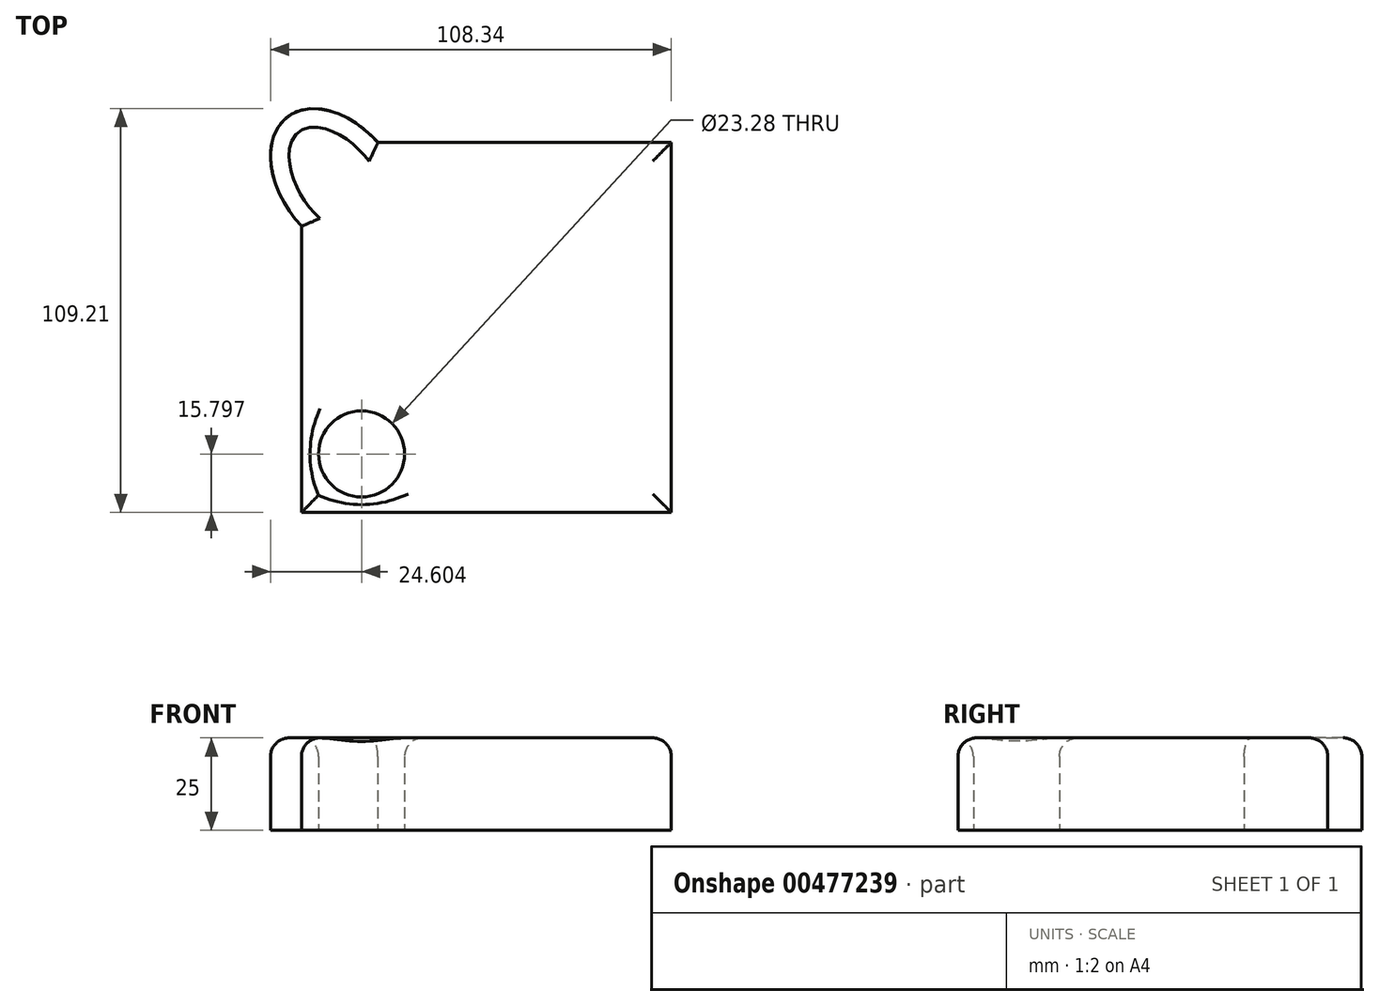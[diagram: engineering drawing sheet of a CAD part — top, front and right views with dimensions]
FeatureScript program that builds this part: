
annotation { "Feature Type Name" : "Feature", "Feature Type Description" : "" }
export const myFeature = defineFeature(function(context is Context, id is Id, definition is map)
    precondition{}
    {
        {
            var Q0;
            Q0=qCreatedBy(makeId("Top.planeOp"),FACE);
            var sketch = newSketch(context, id + "F0", { "sketchPlane" : qUnion([Q0])});
            skLineSegment(sketch, "E0.bottom", {"start": v(-35.24, -50.27) * mm, "end": v(64.76, -50.27) * mm});
            skLineSegment(sketch, "E0.top", {"start": v(-35.24, 49.73) * mm, "end": v(64.76, 49.73) * mm});
            skLineSegment(sketch, "E0.left", {"start": v(-35.24, -50.27) * mm, "end": v(-35.24, 49.73) * mm});
            skLineSegment(sketch, "E0.right", {"start": v(64.76, -50.27) * mm, "end": v(64.76, 49.73) * mm});
            skSolve(sketch);
        }
        {
            var Q0;
            Q0=makeQuery(id+"F0.imprint","IMPRINT",FACE,{"disambiguationData":[TD([[makeQuery(id+"F0.imprint","IMPRINT",EDGE,{"derivedFrom":sQuery(id+"F0.wireOp",EDGE,"E0.bottom")}),1.0]])]});
            extrude(context, id + "F1", {"entities" : qUnion([Q0]), "depth" : 25 * mm});
        }
        {
            var Q0;
            Q0=qCreatedBy(makeId("Top.planeOp"),FACE);
            var sketch = newSketch(context, id + "F2", { "sketchPlane" : qUnion([Q0])});
            skCircle(sketch, "E1", {"center": v(-18.98, -34.47) * mm, "radius": 11.64 * mm});
            skSolve(sketch);
        }
        {
            var Q0;
            Q0 = qSketchRegion(id + "F2", true);
            extrude(context, id + "F3", {"entities" : qUnion([Q0]), "operationType" : NewBodyOperationType.REMOVE, "endBound" : BoundingType.THROUGH_ALL, "depth" : 25 * mm});
        }
        {
            var Q0;
            Q0=qCreatedBy(makeId("Top.planeOp"),FACE);
            var sketch = newSketch(context, id + "F4", { "sketchPlane" : qUnion([Q0])});
            skEllipse(sketch, "E2", {"center": v(-25.26, 38.83) * mm, "majorRadius": 22.56 * mm, "minorRadius": 15.2 * mm, "majorAxis": v(-0.61, 0.79)});
            skSolve(sketch);
        }
        {
            var Q0;
            Q0 = qSketchRegion(id + "F4", true);
            extrude(context, id + "F5", {"entities" : qUnion([Q0]), "operationType" : NewBodyOperationType.ADD, "depth" : 25 * mm});
        }
        {
            var Q0;
            Q0=makeQuery(id+"F5.boolean.opBoolean","MERGE",FACE,{"derivedFrom":[makeQuery(id+"F1.opExtrude","CAP_FACE",FACE,{"disambiguationData":[OSD([sQuery(id+"F0.wireOp",EDGE,"E0.bottom"),sQuery(id+"F0.wireOp",EDGE,"E0.top"),sQuery(id+"F0.wireOp",EDGE,"E0.left"),sQuery(id+"F0.wireOp",EDGE,"E0.right")])],"isStart":false}),makeQuery(id+"F5.opExtrude","CAP_FACE",FACE,{"disambiguationData":[OSD([sQuery(id+"F4.wireOp",EDGE,"E2")])],"isStart":false})]});
            fillet(context, id + "F6", {"entities" : qUnion([Q0]), "radius" : 5 * mm, "tangentPropagation" : true, "allowEdgeOverflow" : false});
        }
    });
